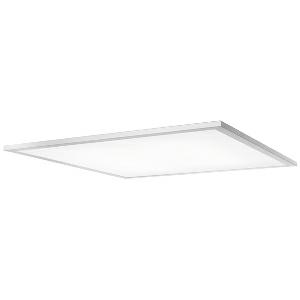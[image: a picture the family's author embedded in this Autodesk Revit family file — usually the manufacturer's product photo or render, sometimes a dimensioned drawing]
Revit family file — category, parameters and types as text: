
# Revit family: dotoo_fit_-_dfe_4000_840_d_sm600_00808118_b3b1
name_source: partatom
category: Lighting Fixtures
units: mm (PartAtom-declared; Revit-internal decimal feet)

## family parameters
Cut with Voids When Loaded = No
Host = Face
Light Source = No
Part Type = Normal
Room Calculation Point = No
Round Connector Dimension = Use Diameter
Shared = No

## types (1)
- DOTOO.fit - DFE 4000/840/D SM600 (1 x LED, 4100 lm, 4000K)
    Apparent Load = 30 VA
    Approval mark = CE
    CIE Flux Codes = 66 90 98 100 100
    Color Rendering = 80-89
    Color Temperature = 4000K
    Control Gear = Electronic ballast
    Default Elevation = 1800 mm
    Description = DFE 4000/840/D|Recessed modular luminaire|light source:  |work equipment: Electronic ballast|connected load: 220-240V, 50/60Hz|Power consumption: approx. 30 W|standby: approx. 0,50|power factor: approx. 0,900|luminous flux: 4100 lm|luminous efficacy: 136 lm/W|light distribution: Direct|direct ratio: approx. 100 %|colour temperature: Cold white, ca. 4000 K|color rendering index (CRI): >= 80|chromaticity tolerance:  3 SDCM|System of protection: IP 20|class of protection: II|technology: Continuously dimmable|operation: External|luminaire body|material: Sectional aluminium|colour: White|weight (net): approx. 2.9 kg|mains lead: 0.50 m Connector|glare control: Prism aperture|luminance(L65): <= 2700 cd/m|unified glare rating(4H 8H): <=  19|special features: DALI Load 1x, TouchDIM - dimming via standard switch, Direct light component with edge light and light-guide technology for homogenous light exit, Flicker-free, System dimension 600 x 600 mm, Strain relief with the possibility of through-wiring|
    Height = 0 mm  [stored 0 ft]
    Lamp = 1 x LED
    Lamp Light Flux = 4100 lm
    Lamp count = 1
    Length = 596 mm
    Luminous efficacy = 137 lm/W
    Manufacturer = Waldmann
    ModVariant = No
    Model = 00808118
    Mounting Place = Ceiling
    Mounting Type = Recessed
    Number of Poles = 1
    OnlyDefault = Yes
    Power Factor = 1
    Product Name = DOTOO.fit - DFE 4000/840/D SM600
    Product group = Recessed luminaire
    ProductGroupID = 4
    Protection Class = Protection class II
    Protection Degree = IP 20
    RLX_Detail_Level = 1
    RLX_Emergency_Light_Flux = 0 lm
    RLX_Emergency_Type = 0
    RLX_Emergency_Type_DB = No
    RlxData = <blob elided: 37701 chars, md5=ad349701>
    Socket = socket
    Standby Power = 0 W
    System Light Flux = 4100 lm
    System Power = 30 W
    Type Comments = Product without accessories
    Type Image = 113328000-00692486.jpg
    URL = http://relux.com
    VarID = ---
    Voltage = 230 V
    Voltage Range = 220-240 V
    Weight = 0.00 kg
    Width = 596 mm

note: [stored X ft] marks values corroborated as IEEE doubles in the binary element streams (Revit-internal decimal feet)

## geometry (parser evidence)
native form markers: Blend x4, Sweep x10
no freeform markers — native parametric forms only
